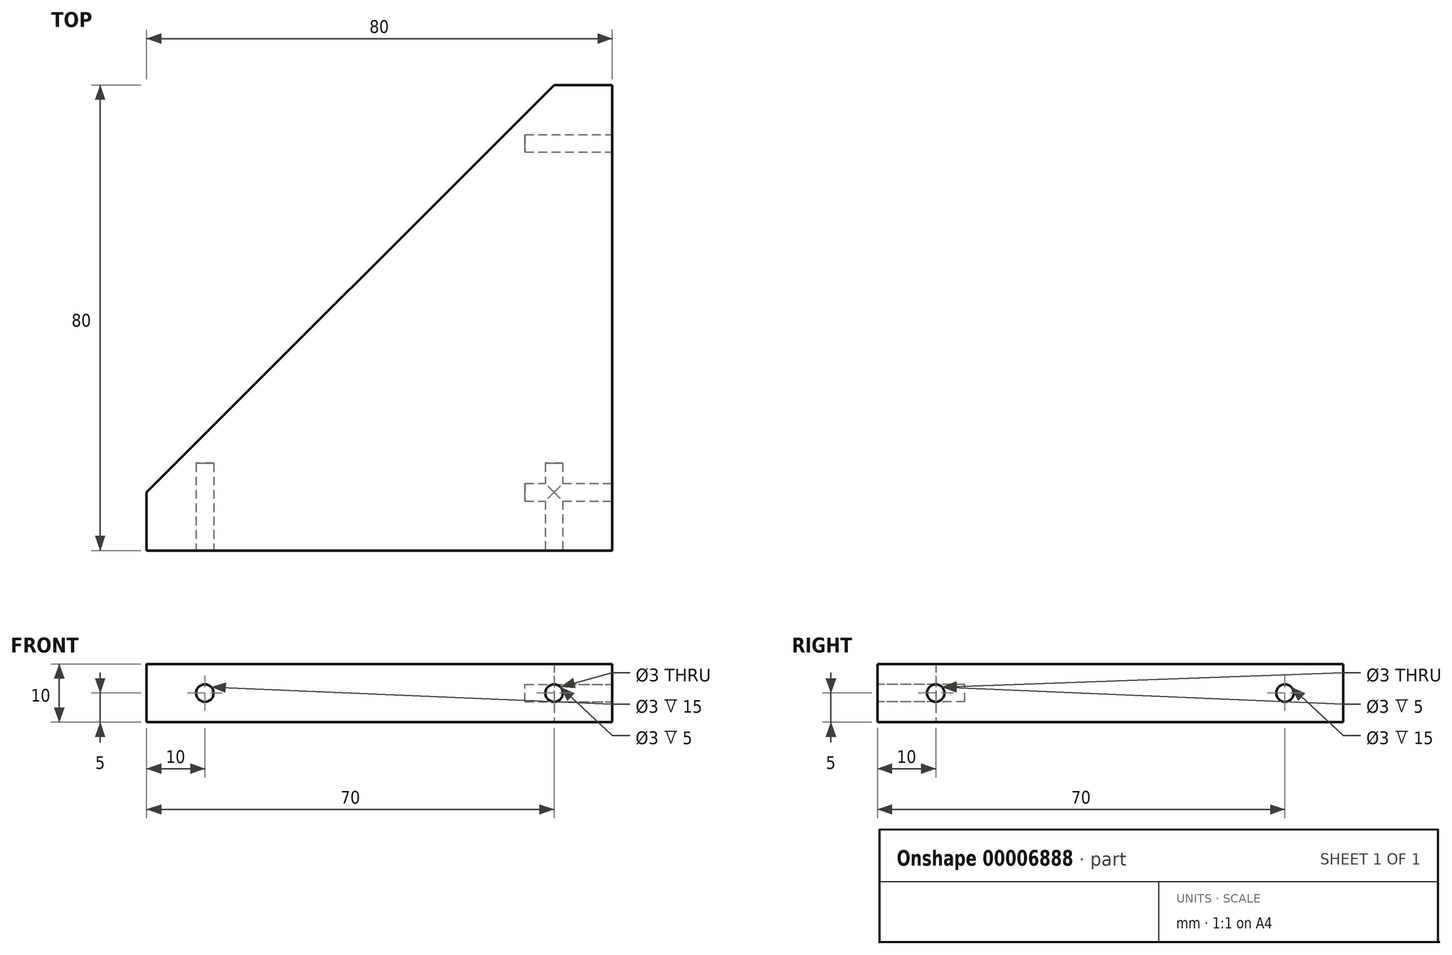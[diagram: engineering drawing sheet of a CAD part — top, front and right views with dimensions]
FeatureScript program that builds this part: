
annotation { "Feature Type Name" : "Feature", "Feature Type Description" : "" }
export const myFeature = defineFeature(function(context is Context, id is Id, definition is map)
    precondition{}
    {
        {
            var Q0;
            Q0=qCreatedBy(makeId("Top.planeOp"),FACE);
            var sketch = newSketch(context, id + "F0", { "sketchPlane" : qUnion([Q0])});
            skLineSegment(sketch, "E0", {"start": v(0, 0) * mm, "end": v(0, 80) * mm});
            skLineSegment(sketch, "E1", {"start": v(0, 80) * mm, "end": v(-10, 80) * mm});
            skLineSegment(sketch, "E2", {"start": v(-10, 80) * mm, "end": v(-80, 10) * mm});
            skLineSegment(sketch, "E3", {"start": v(-80, 10) * mm, "end": v(-80, 0) * mm});
            skLineSegment(sketch, "E4", {"start": v(-80, 0) * mm, "end": v(0, 0) * mm});
            skSolve(sketch);
        }
        {
            var Q0;
            Q0 = qSketchRegion(id + "F0", true);
            extrude(context, id + "F1", {"entities" : qUnion([Q0]), "depth" : (10) * mm});
        }
        {
            var Q0;
            Q0=makeQuery(id+"F1.opExtrude","SWEPT_FACE",FACE,{"disambiguationData":[OSD([sQuery(id+"F0.wireOp",EDGE,"E4")])]});
            var sketch = newSketch(context, id + "F2", { "sketchPlane" : qUnion([Q0])});
            skLineSegment(sketch, "E5", {"start": v(-80, 5) * mm, "end": v(0, 5) * mm, "construction": true});
            skCircle(sketch, "E6", {"center": v(-70, 5) * mm, "radius": 1.5 * mm});
            skCircle(sketch, "E7", {"center": v(-10, 5) * mm, "radius": 1.5 * mm});
            skSolve(sketch);
        }
        {
            var Q0;
            Q0 = qSketchRegion(id + "F2", true);
            extrude(context, id + "F3", {"entities" : qUnion([Q0]), "operationType" : NewBodyOperationType.REMOVE, "oppositeDirection" : true, "depth" : (15) * mm});
        }
        {
            var Q0;
            Q0=makeQuery(id+"F1.opExtrude","SWEPT_FACE",FACE,{"disambiguationData":[OSD([sQuery(id+"F0.wireOp",EDGE,"E0")])]});
            var sketch = newSketch(context, id + "F4", { "sketchPlane" : qUnion([Q0])});
            skLineSegment(sketch, "E8", {"start": v(0, 5) * mm, "end": v(80, 5) * mm, "construction": true});
            skCircle(sketch, "E9", {"center": v(10, 5) * mm, "radius": 1.5 * mm});
            skCircle(sketch, "E10", {"center": v(70, 5) * mm, "radius": 1.5 * mm});
            skSolve(sketch);
        }
        {
            var Q0;
            Q0 = qSketchRegion(id + "F4", true);
            extrude(context, id + "F5", {"entities" : qUnion([Q0]), "operationType" : NewBodyOperationType.REMOVE, "oppositeDirection" : true, "depth" : (15) * mm});
        }
    });
